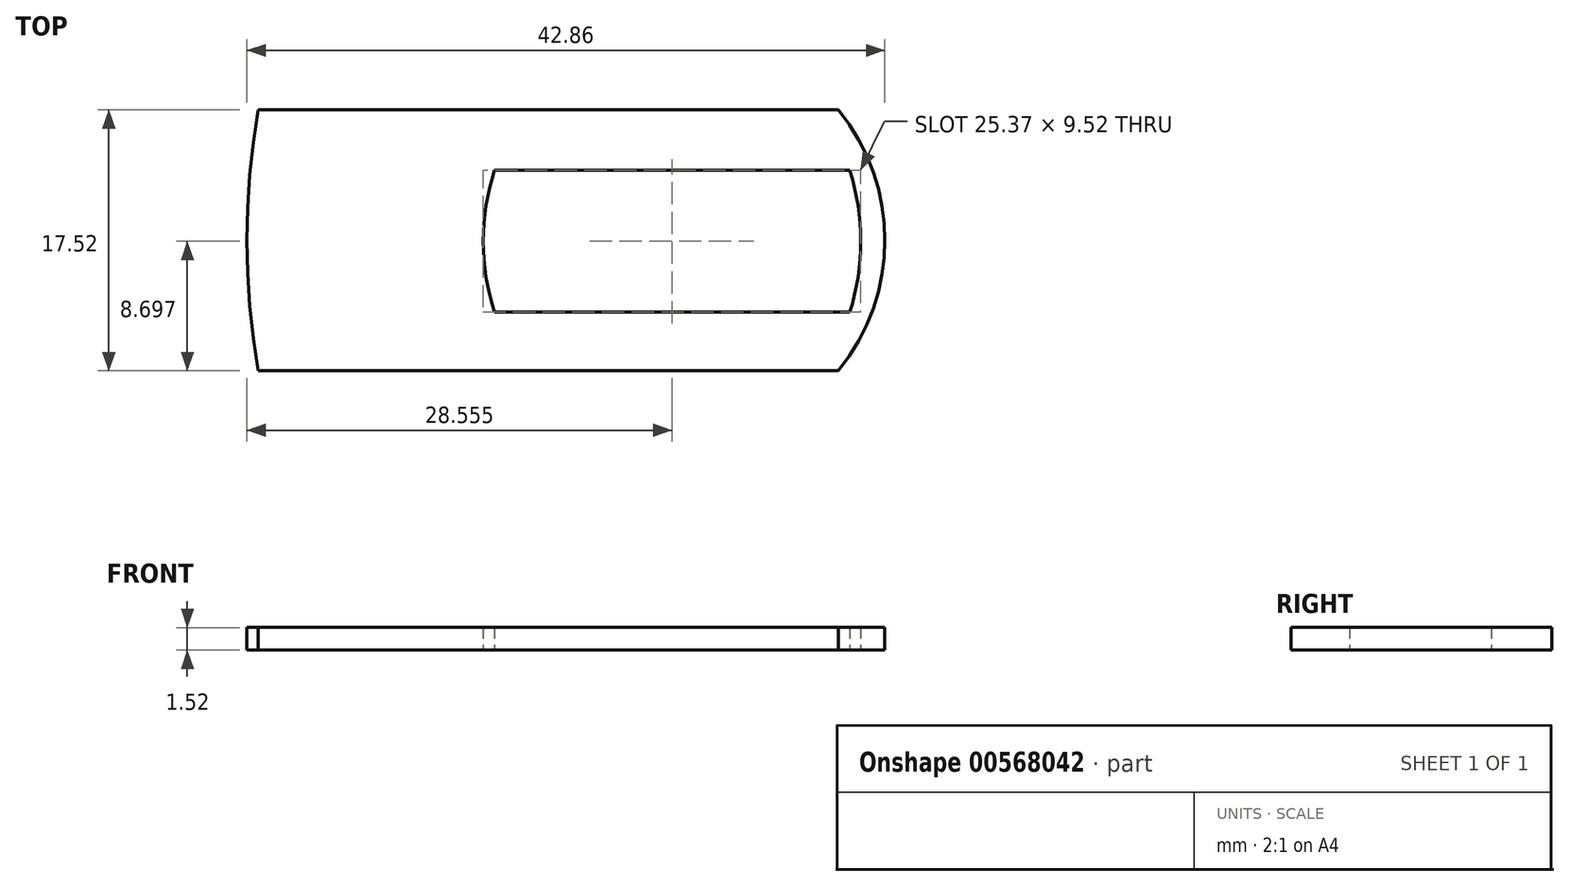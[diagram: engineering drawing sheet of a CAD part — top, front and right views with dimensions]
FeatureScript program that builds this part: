
annotation { "Feature Type Name" : "Feature", "Feature Type Description" : "" }
export const myFeature = defineFeature(function(context is Context, id is Id, definition is map)
    precondition{}
    {
        {
            var Q0;
            Q0=qCreatedBy(makeId("Top.planeOp"),FACE);
            var sketch = newSketch(context, id + "F0", { "sketchPlane" : qUnion([Q0])});
            skLineSegment(sketch, "E0.bottom", {"start": v(18.29, 8.76) * mm, "end": v(-21.46, 8.76) * mm});
            skLineSegment(sketch, "E0.top", {"start": v(18.29, -8.76) * mm, "end": v(-21.46, -8.76) * mm});
            skPoint(sketch, "E0.middle", {"position": v(0, 0) * mm});
            skLineSegment(sketch, "E1", {"start": v(-21.46, 8.76) * mm, "end": v(-20.7, 8.76) * mm});
            skLineSegment(sketch, "E2", {"start": v(-21.46, -8.76) * mm, "end": v(-20.7, -8.76) * mm});
            skPoint(sketch, "E3.visualSharp", {"position": v(-21.46, 0) * mm});
            skArc(sketch, "E4", {"start": v(-20.7, 8.76) * mm, "mid": v(-21.46, 0) * mm, "end": v(-20.7, -8.76) * mm});
            skLineSegment(sketch, "E5", {"start": v(-21.46, 0) * mm, "end": v(-5.59, 0) * mm});
            skLineSegment(sketch, "E6", {"start": v(19.81, 4.7) * mm, "end": v(19.05, 4.7) * mm});
            skLineSegment(sketch, "E7", {"start": v(19.81, -4.83) * mm, "end": v(19.05, -4.83) * mm});
            skArc(sketch, "E8", {"start": v(19.05, -4.83) * mm, "mid": v(19.78, -0.06) * mm, "end": v(19.05, 4.7) * mm});
            skPoint(sketch, "E9.visualSharp", {"position": v(21.46, 8.76) * mm});
            skPoint(sketch, "E10.visualSharp", {"position": v(21.46, -8.76) * mm});
            skArc(sketch, "E11", {"start": v(18.29, -8.76) * mm, "mid": v(21.4, 0) * mm, "end": v(18.29, 8.76) * mm});
            skLineSegment(sketch, "E12", {"start": v(-5.59, -4.83) * mm, "end": v(-4.83, -4.83) * mm});
            skLineSegment(sketch, "E13", {"start": v(-5.59, 4.7) * mm, "end": v(-4.83, 4.7) * mm});
            skArc(sketch, "E14", {"start": v(-4.83, 4.7) * mm, "mid": v(-5.59, -0.06) * mm, "end": v(-4.83, -4.83) * mm});
            skLineSegment(sketch, "E15", {"start": v(-4.83, 4.7) * mm, "end": v(19.05, 4.7) * mm});
            skLineSegment(sketch, "E16", {"start": v(-4.83, -4.83) * mm, "end": v(19.05, -4.83) * mm});
            skSolve(sketch);
        }
        {
            var Q0;
            {var subQ3=sQuery(id+"F0.wireOp",EDGE,"E0.bottom");Q0=makeQuery(id+"F0.imprint","IMPRINT",FACE,{"disambiguationData":[TD([[makeQuery(id+"F0.imprint","IMPRINT",EDGE,{"derivedFrom":subQ3}),1.0]])]});}
            extrude(context, id + "F1", {"entities" : qUnion([Q0]), "depth" : 1.52 * mm, "offsetDistance" : 25.4 * mm});
        }
    });
